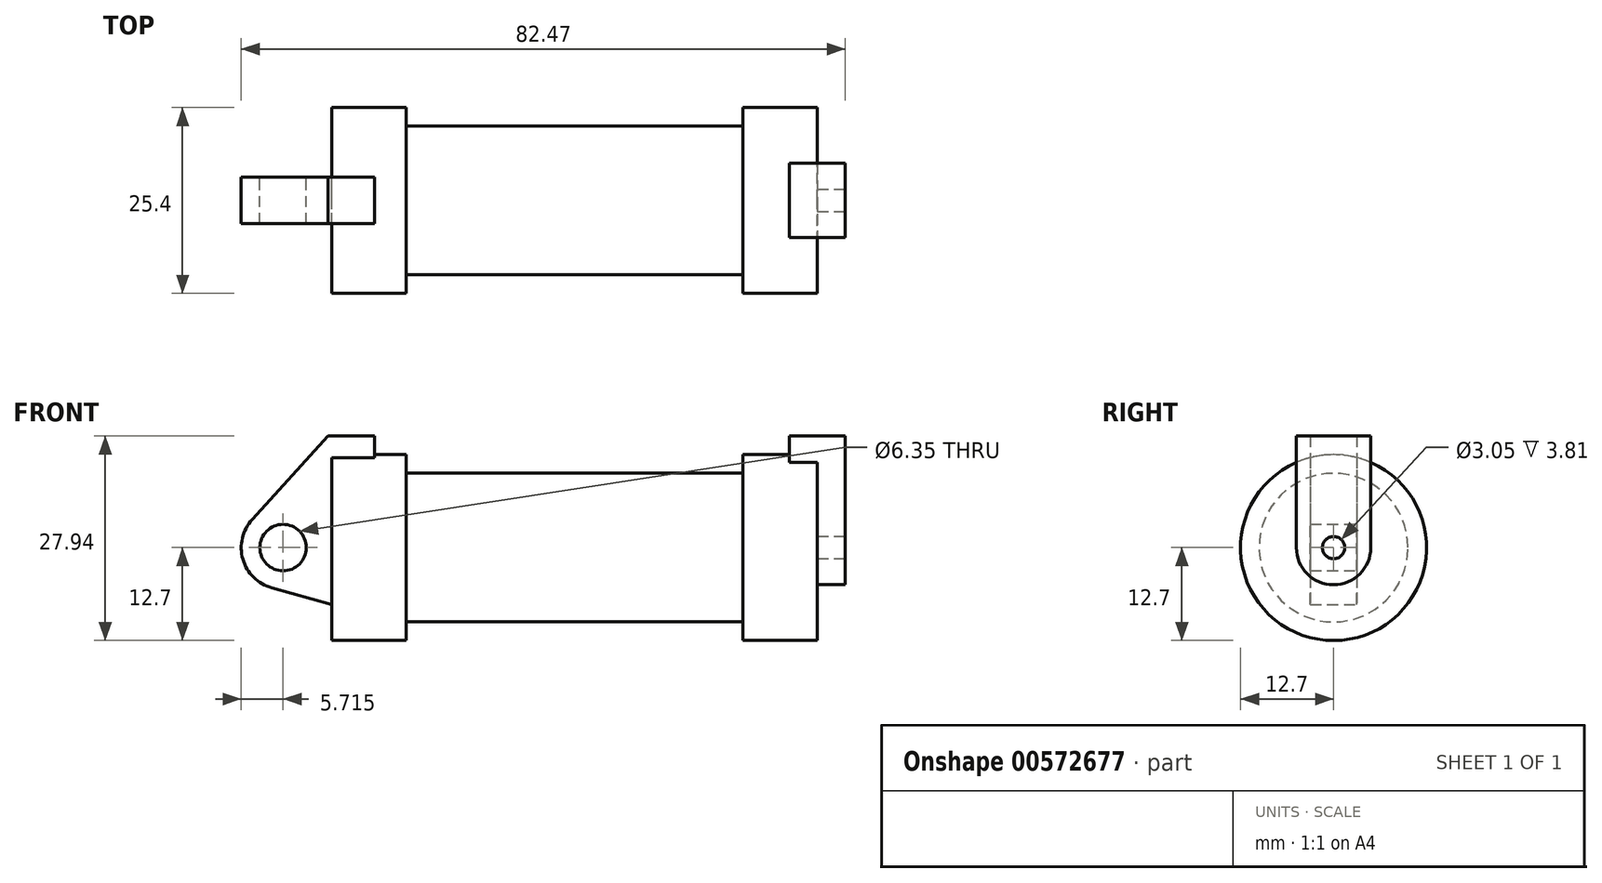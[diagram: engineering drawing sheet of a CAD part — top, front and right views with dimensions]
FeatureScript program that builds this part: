
annotation { "Feature Type Name" : "Feature", "Feature Type Description" : "" }
export const myFeature = defineFeature(function(context is Context, id is Id, definition is map)
    precondition{}
    {
        {
            var Q0;
            Q0=qCreatedBy(makeId("Front.planeOp"),FACE);
            var sketch = newSketch(context, id + "F0", { "sketchPlane" : qUnion([Q0])});
            skLineSegment(sketch, "E0", {"start": v(0, 0) * mm, "end": v(0, 12.7) * mm});
            skLineSegment(sketch, "E1", {"start": v(0, 12.7) * mm, "end": v(10.16, 12.7) * mm});
            skLineSegment(sketch, "E2", {"start": v(10.16, 12.7) * mm, "end": v(10.16, 10.16) * mm});
            skLineSegment(sketch, "E3", {"start": v(10.16, 10.16) * mm, "end": v(56.13, 10.16) * mm});
            skLineSegment(sketch, "E4", {"start": v(56.13, 10.16) * mm, "end": v(56.13, 12.7) * mm});
            skLineSegment(sketch, "E5", {"start": v(56.13, 12.7) * mm, "end": v(66.3, 12.7) * mm});
            skLineSegment(sketch, "E6", {"start": v(66.3, 12.7) * mm, "end": v(66.3, 0) * mm});
            skLineSegment(sketch, "E7", {"start": v(66.3, 0) * mm, "end": v(0, 0) * mm});
            skLineSegment(sketch, "E8", {"start": v(5.84, 15.24) * mm, "end": v(-0.5, 15.24) * mm});
            skLineSegment(sketch, "E9", {"start": v(-0.5, 15.24) * mm, "end": v(-10.88, 3.85) * mm});
            skLineSegment(sketch, "E10", {"start": v(0, 0) * mm, "end": v(-6.65, 0) * mm});
            skCircle(sketch, "E11", {"center": v(-6.65, 0) * mm, "radius": 5.72 * mm});
            skCircle(sketch, "E12", {"center": v(-6.65, 0) * mm, "radius": 3.18 * mm});
            skLineSegment(sketch, "E13", {"start": v(5.84, 15.24) * mm, "end": v(5.84, -9.4) * mm});
            skLineSegment(sketch, "E14", {"start": v(5.84, -9.4) * mm, "end": v(-8.18, -5.5) * mm});
            skSolve(sketch);
        }
        {
            var Q0;
            {var subQ0=sQuery(id+"F0.wireOp",EDGE,"E2");Q0=makeQuery(id+"F0.imprint","IMPRINT",FACE,{"disambiguationData":[TD([[makeQuery(id+"F0.imprint","IMPRINT",EDGE,{"derivedFrom":subQ0}),-1.0]])]});}
            var Q1;
            {var subQ0=sQuery(id+"F0.wireOp",EDGE,"E0");Q1=makeQuery(id+"F0.imprint","IMPRINT",FACE,{"disambiguationData":[TD([[makeQuery(id+"F0.imprint","IMPRINT",EDGE,{"derivedFrom":subQ0}),-1.0]])]});}
            var Q2;
            Q2=sQuery(id+"F0.wireOp",EDGE,"E7");
            revolve(context, id + "F1", {"entities" : qUnion([Q0, Q1]), "axis" : qUnion([Q2]), "revolveType" : RevolveType.FULL});
        }
        {
            var Q0;
            {var subQ5=sQuery(id+"F0.wireOp",EDGE,"E12");Q0=makeQuery(id+"F0.imprint","IMPRINT",FACE,{"disambiguationData":[TD([[makeQuery(id+"F0.imprint","IMPRINT",EDGE,{"derivedFrom":subQ5}),-1.0]])]});}
            var Q1;
            {var subQ0=sQuery(id+"F0.wireOp",EDGE,"E0");Q1=makeQuery(id+"F0.imprint","IMPRINT",FACE,{"disambiguationData":[TD([[makeQuery(id+"F0.imprint","IMPRINT",EDGE,{"derivedFrom":subQ0}),-1.0]])]});}
            var Q2;
            {var subQ1=sQuery(id+"F0.wireOp",EDGE,"E0");Q2=makeQuery(id+"F0.imprint","IMPRINT",FACE,{"disambiguationData":[TD([[makeQuery(id+"F0.imprint","IMPRINT",EDGE,{"derivedFrom":subQ1}),1.0]])]});}
            var Q3;
            {var subQ0=sQuery(id+"F0.wireOp",EDGE,"E14");Q3=makeQuery(id+"F0.imprint","IMPRINT",FACE,{"disambiguationData":[TD([[makeQuery(id+"F0.imprint","IMPRINT",EDGE,{"derivedFrom":subQ0}),-1.0]])]});}
            extrude(context, id + "F2", {"entities" : qUnion([Q0, Q1, Q2, Q3]), "operationType" : NewBodyOperationType.ADD, "endBound" : BoundingType.SYMMETRIC, "depth" : 6.35 * mm, "offsetDistance" : 25.4 * mm});
        }
        {
            var Q0;
            Q0=makeQuery(id+"F1.opRevolve","SWEPT_FACE",FACE,{"disambiguationData":[OSD([sQuery(id+"F0.wireOp",EDGE,"E6")])]});
            var sketch = newSketch(context, id + "F3", { "sketchPlane" : qUnion([Q0])});
            skCircle(sketch, "E15", {"center": v(0, 0) * mm, "radius": 1.52 * mm});
            skCircle(sketch, "E16", {"center": v(0, 0) * mm, "radius": 5.08 * mm});
            skLineSegment(sketch, "E17", {"start": v(5.08, 0) * mm, "end": v(5.08, 15.24) * mm});
            skLineSegment(sketch, "E18", {"start": v(-5.08, 0) * mm, "end": v(-5.08, 15.24) * mm});
            skLineSegment(sketch, "E19", {"start": v(-5.08, 15.24) * mm, "end": v(5.08, 15.24) * mm});
            skSolve(sketch);
        }
        {
            var Q0;
            Q0 = qSketchRegion(id + "F3", true);
            extrude(context, id + "F4", {"entities" : qUnion([Q0]), "operationType" : NewBodyOperationType.ADD, "endBound" : BoundingType.SYMMETRIC, "oppositeDirection" : true, "depth" : 7.62 * mm, "offsetDistance" : 25.4 * mm});
        }
    });
